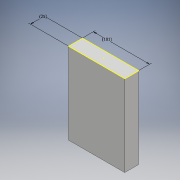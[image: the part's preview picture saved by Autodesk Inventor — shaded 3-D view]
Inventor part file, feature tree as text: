
AUTODESK INVENTOR PART (.ipt)
format: ipt  version: 2017 (Build 210142000, 142)  size: 96,256 bytes
history: native  units: mm
features: sketch x2, extrude x1, projected_geometry x1
ambient origin geometry x8: Origin, YZ Plane, XZ Plane, XY Plane, X Axis, Y Axis, Z Axis, Center Point
bodies: Solid1 (feature_tree)
feature tree (4):
  extrude  "Extrusion1"  Depth=25.0mm
  sketch  "Sketch2"  dims[d2=146.0mm d3=0.0mm d4=101.0mm d5=25.0mm]
  sketch  "Sketch1"  dims[d0=101.0mm d1=25.0mm]
  projected_geometry  "Projected Loop1"
